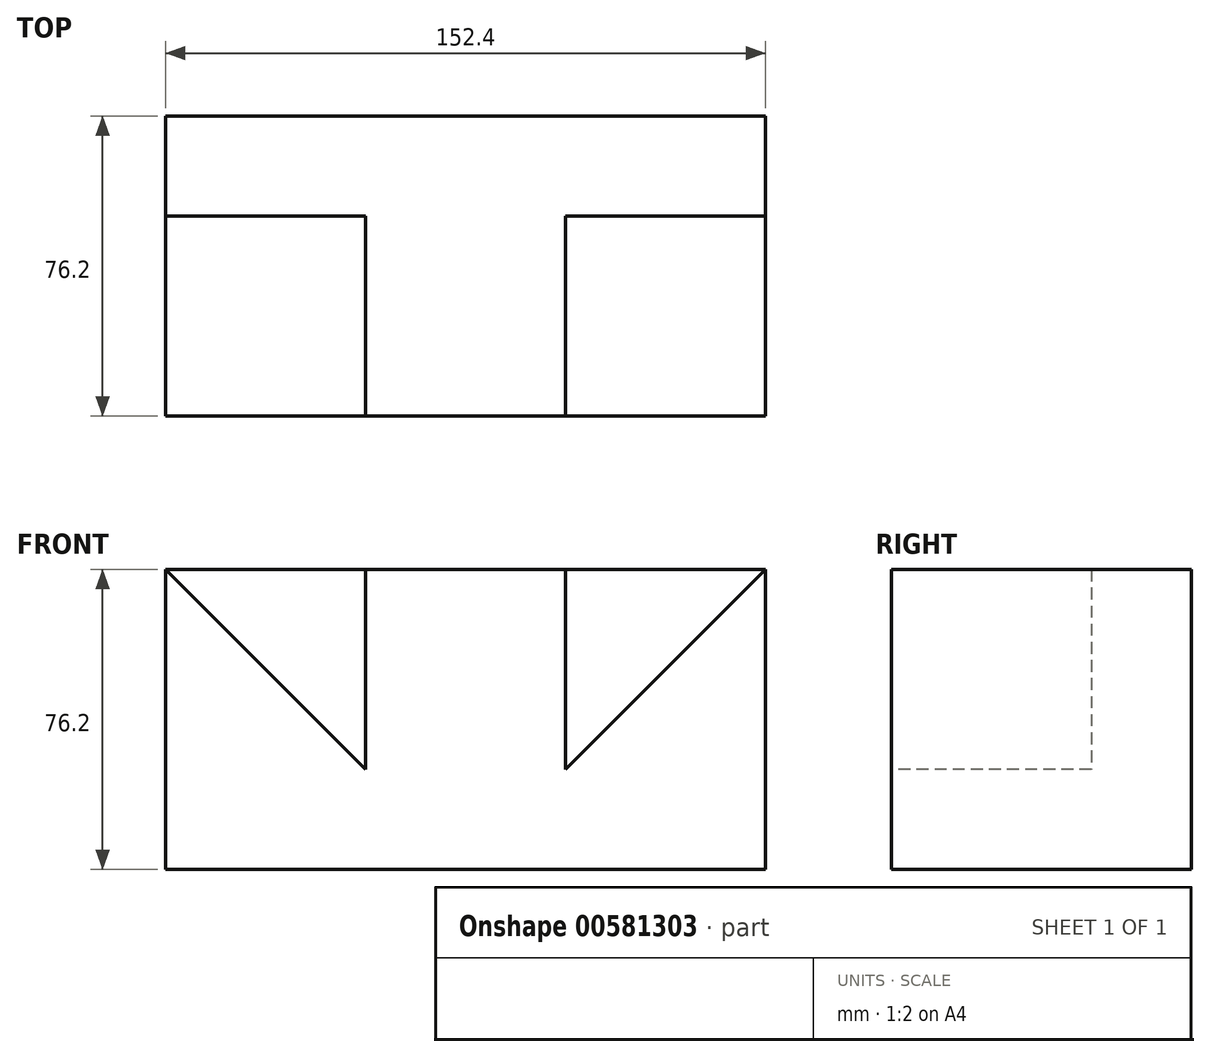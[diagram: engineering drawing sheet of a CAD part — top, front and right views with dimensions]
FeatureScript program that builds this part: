
annotation { "Feature Type Name" : "Feature", "Feature Type Description" : "" }
export const myFeature = defineFeature(function(context is Context, id is Id, definition is map)
    precondition{}
    {
        {
            var Q0;
            Q0=qCreatedBy(makeId("Top.planeOp"),FACE);
            var sketch = newSketch(context, id + "F0", { "sketchPlane" : qUnion([Q0])});
            skLineSegment(sketch, "E0.bottom", {"start": v(-74.54, 2.76) * mm, "end": v(77.86, 2.76) * mm});
            skLineSegment(sketch, "E0.top", {"start": v(-74.54, -73.44) * mm, "end": v(77.86, -73.44) * mm});
            skLineSegment(sketch, "E0.left", {"start": v(-74.54, 2.76) * mm, "end": v(-74.54, -73.44) * mm});
            skLineSegment(sketch, "E0.right", {"start": v(77.86, 2.76) * mm, "end": v(77.86, -73.44) * mm});
            skSolve(sketch);
        }
        {
            var Q0;
            Q0=qSketchRegion(id+"F0",true);
            extrude(context, id + "F1", {"entities" : qUnion([Q0]), "depth" : 101.6 * mm, "offsetDistance" : 25.4 * mm});
        }
        {
            var Q0;
            Q0=makeQuery(id+"F1.opExtrude","SWEPT_FACE",FACE,{"disambiguationData":[OSD([sQuery(id+"F0.wireOp",EDGE,"E0.right")])]});
            var sketch = newSketch(context, id + "F2", { "sketchPlane" : qUnion([Q0])});
            skLineSegment(sketch, "E1.bottom", {"start": v(-73.44, 0) * mm, "end": v(2.76, 0) * mm});
            skLineSegment(sketch, "E1.top", {"start": v(-73.44, 76.2) * mm, "end": v(2.76, 76.2) * mm});
            skLineSegment(sketch, "E1.left", {"start": v(-73.44, 0) * mm, "end": v(-73.44, 76.2) * mm});
            skLineSegment(sketch, "E1.right", {"start": v(2.76, 0) * mm, "end": v(2.76, 76.2) * mm});
            skLineSegment(sketch, "E2.bottom", {"start": v(2.76, 101.6) * mm, "end": v(-22.64, 101.6) * mm});
            skLineSegment(sketch, "E2.top", {"start": v(2.76, 76.2) * mm, "end": v(-22.64, 76.2) * mm});
            skLineSegment(sketch, "E2.left", {"start": v(2.76, 101.6) * mm, "end": v(2.76, 76.2) * mm});
            skLineSegment(sketch, "E2.right", {"start": v(-22.64, 101.6) * mm, "end": v(-22.64, 76.2) * mm});
            skSolve(sketch);
        }
        {
            var Q0;
            {var subQ0=sQuery(id+"F2.wireOp",EDGE,"E1.top");Q0=makeQuery(id+"F2.imprint","IMPRINT",FACE,{"disambiguationData":[TD([[makeQuery(id+"F2.imprint","IMPRINT",EDGE,{"derivedFrom":subQ0}),1.0]])]});}
            extrude(context, id + "F3", {"entities" : qUnion([Q0]), "operationType" : NewBodyOperationType.REMOVE, "oppositeDirection" : true, "depth" : 152.4 * mm, "offsetDistance" : 25.4 * mm});
        }
        {
            var Q0;
            Q0=makeQuery(id+"F1.opExtrude","SWEPT_FACE",FACE,{"disambiguationData":[OSD([sQuery(id+"F0.wireOp",EDGE,"E0.top")])]});
            var sketch = newSketch(context, id + "F4", { "sketchPlane" : qUnion([Q0])});
            skLineSegment(sketch, "E3.bottom", {"start": v(-74.54, 76.2) * mm, "end": v(-23.74, 76.2) * mm});
            skLineSegment(sketch, "E3.top", {"start": v(-74.54, 0) * mm, "end": v(-23.74, 0) * mm});
            skLineSegment(sketch, "E3.left", {"start": v(-74.54, 76.2) * mm, "end": v(-74.54, 0) * mm});
            skLineSegment(sketch, "E3.right", {"start": v(-23.74, 76.2) * mm, "end": v(-23.74, 0) * mm});
            skLineSegment(sketch, "E4.top", {"start": v(-23.74, 0) * mm, "end": v(27.06, 0) * mm});
            skLineSegment(sketch, "E4.right", {"start": v(27.06, 76.2) * mm, "end": v(27.06, 0) * mm});
            skLineSegment(sketch, "E5.bottom", {"start": v(27.06, 76.2) * mm, "end": v(77.86, 76.2) * mm});
            skLineSegment(sketch, "E5.top", {"start": v(27.06, 0) * mm, "end": v(77.86, 0) * mm});
            skLineSegment(sketch, "E5.right", {"start": v(77.86, 76.2) * mm, "end": v(77.86, 0) * mm});
            skLineSegment(sketch, "E6.left", {"start": v(-23.74, 25.4) * mm, "end": v(-23.74, 0) * mm});
            skLineSegment(sketch, "E6.right", {"start": v(27.06, 41.25) * mm, "end": v(27.06, 0) * mm});
            skLineSegment(sketch, "E7.bottom", {"start": v(-23.74, 25.4) * mm, "end": v(27.06, 25.4) * mm});
            skLineSegment(sketch, "E7.right", {"start": v(27.06, 25.4) * mm, "end": v(27.06, 0) * mm});
            skLineSegment(sketch, "E8", {"start": v(-74.54, 76.2) * mm, "end": v(-23.74, 25.4) * mm});
            skLineSegment(sketch, "E9", {"start": v(27.06, 25.4) * mm, "end": v(77.86, 76.2) * mm});
            skSolve(sketch);
        }
        {
            var Q0;
            Q0=makeQuery(id+"F4.imprint","IMPRINT",FACE,{"disambiguationData":[TD([[makeQuery(id+"F4.imprint","IMPRINT",EDGE,{"derivedFrom":sQuery(id+"F4.wireOp",EDGE,"E5.bottom")}),-1.0]])]});
            var Q1;
            {var subQ1=sQuery(id+"F4.wireOp",EDGE,"E3.right");Q1=makeQuery(id+"F4.imprint","IMPRINT",FACE,{"disambiguationData":[TD([[makeQuery(id+"F4.imprint","IMPRINT",EDGE,{"derivedFrom":subQ1}),1.0]])]});}
            var Q2;
            Q2=makeQuery(id+"F4.imprint","IMPRINT",FACE,{"disambiguationData":[TD([[makeQuery(id+"F4.imprint","IMPRINT",EDGE,{"derivedFrom":sQuery(id+"F4.wireOp",EDGE,"E3.bottom")}),-1.0]])]});
            extrude(context, id + "F5", {"entities" : qUnion([Q0, Q1, Q2]), "operationType" : NewBodyOperationType.REMOVE, "oppositeDirection" : true, "depth" : 50.8 * mm, "offsetDistance" : 25.4 * mm});
        }
    });
